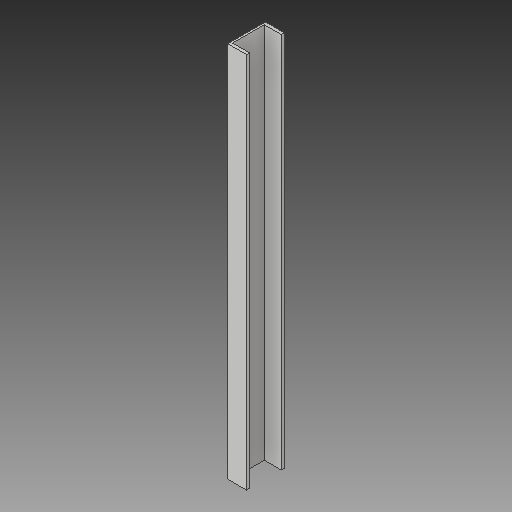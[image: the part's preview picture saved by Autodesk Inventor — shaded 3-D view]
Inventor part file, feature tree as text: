
AUTODESK INVENTOR PART (.ipt)
format: ipt  version: 2019 (Build 230136000, 136)  size: 87,040 bytes
history: native  units: in
note: dims shown in document units (in); Inventor stores cm internally (conversion verified against a paired STEP export)
features: other x3, sketch x1
ambient origin geometry x8: Origin, YZ Plane, XZ Plane, XY Plane, X Axis, Y Axis, Z Axis, Center Point
bodies: Solid1 (feature_tree)
feature tree (4):
  other  "Channel1_MIR_MIR.ipt"
  other  "Solid1::Channel1_MIR_MIR.ipt"
  other  "TaggingFeature1"
  sketch  "Sketch1"  dims[d0=0.3937in]
